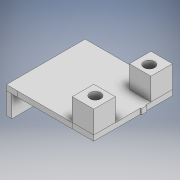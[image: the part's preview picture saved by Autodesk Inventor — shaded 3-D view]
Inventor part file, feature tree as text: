
AUTODESK INVENTOR PART (.ipt)
format: ipt  version: 2020 (Build 240168000, 168)  size: 183,296 bytes
history: native  units: mm
features: sketch x9, extrude x8
ambient origin geometry x8: Origin, YZ Plane, XZ Plane, XY Plane, X Axis, Y Axis, Z Axis, Center Point
bodies: Solid1 (feature_tree)
feature tree (17):
  sketch  "Sketch1"  dims[d4=10.0mm d6=2.0mm]
  sketch  "Sketch2"  dims[d7=2.0mm d8=2.3mm]
  extrude  "Extrusion1"  Depth=2.0mm
  extrude  "Extrusion2"  Depth=2.0mm
  extrude  "Extrusion3"  Depth=7.3mm
  sketch  "Sketch4"  dims[d14=1.7mm d15=1.7mm]
  extrude  "Extrusion4"  Depth=1.7mm
  extrude  "Extrusion5"  Depth=1.0mm TaperAngle=0.0deg
  extrude  "Extrusion6"  Depth=2.0mm
  extrude  "Extrusion7"  Depth=2.0mm
  extrude  "Extrusion8"  Depth=2.0mm TaperAngle=0.0deg
  sketch  "Sketch3"  dims[d9=14.2mm d10=7.3mm]
  sketch  "Sketch5"  dims[d16=4.15mm d17=0.0mm d18=1.0mm d19=0.0mm]
  sketch  "Sketch6"  dims[d20=4.0mm d21=0.0mm d22=2.0mm]
  sketch  "Sketch7"  dims[d23=1.0mm d24=0.0mm d25=2.0mm]
  sketch  "Sketch10"  dims[d26=1.0mm d27=0.0mm d28=2.0mm d29=0.0mm]
  sketch  "Sketch11"  dims[d31=1.0mm d32=4.0mm d33=0.0mm d34=0.5mm d35=1.0mm d36=0.2mm d37=0.0mm]
